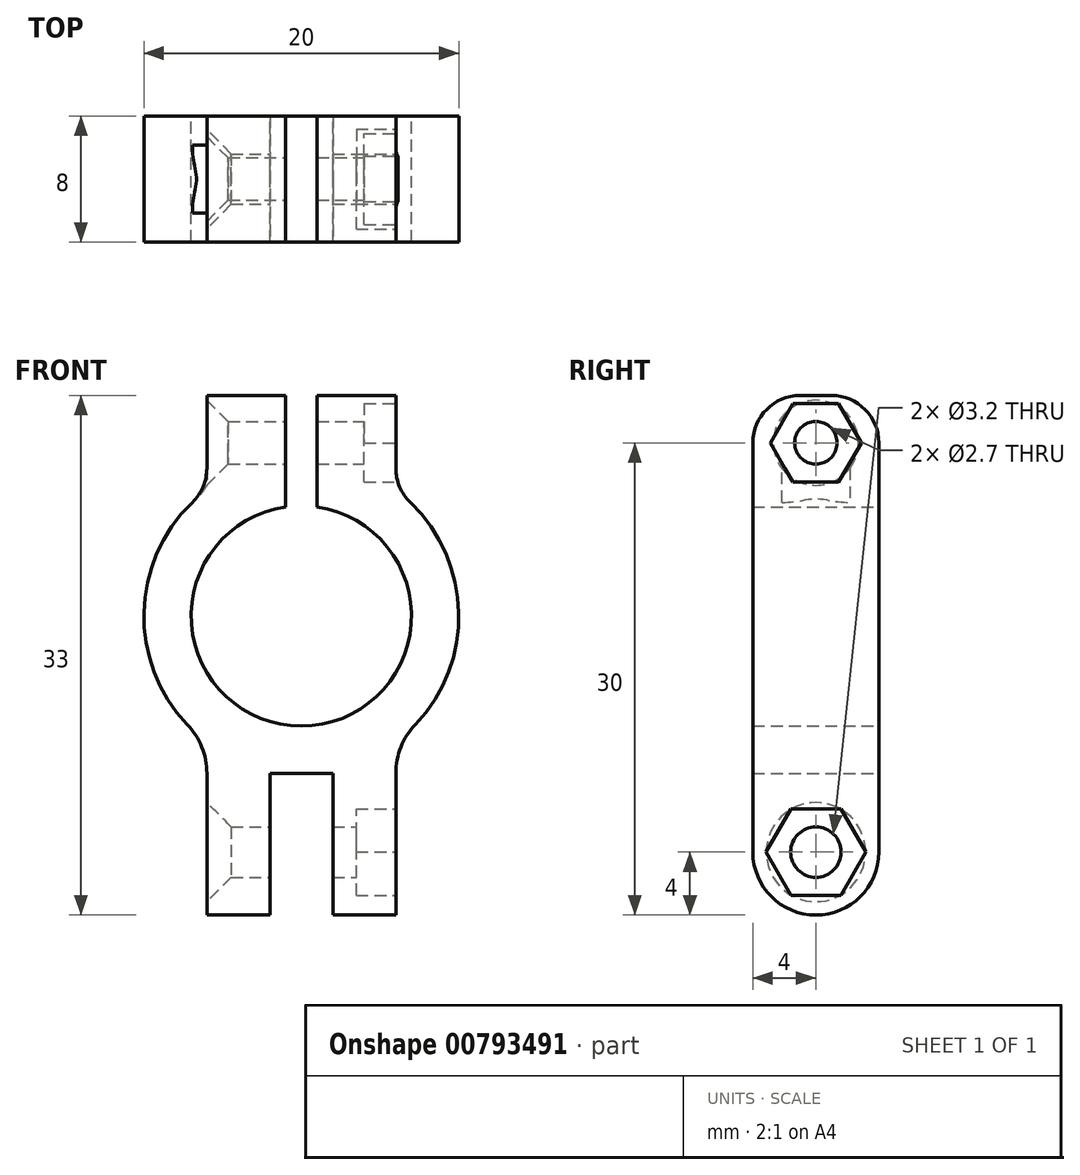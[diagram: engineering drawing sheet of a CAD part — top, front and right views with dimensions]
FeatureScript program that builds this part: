
annotation { "Feature Type Name" : "Feature", "Feature Type Description" : "" }
export const myFeature = defineFeature(function(context is Context, id is Id, definition is map)
    precondition{}
    {
        {
            var Q0;
            Q0=qCreatedBy(makeId("Front.planeOp"),FACE);
            var sketch = newSketch(context, id + "F0", { "sketchPlane" : qUnion([Q0])});
            skLineSegment(sketch, "E0", {"start": v(-1, 14) * mm, "end": v(-1, 6.93) * mm});
            skLineSegment(sketch, "E1.trimOffspring", {"start": v(-1, 14) * mm, "end": v(-6, 14) * mm});
            skLineSegment(sketch, "E2", {"start": v(-6, -19) * mm, "end": v(-2, -19) * mm});
            skLineSegment(sketch, "E3", {"start": v(-2, -19) * mm, "end": v(-2, -10) * mm});
            skLineSegment(sketch, "E4", {"start": v(-6, -19) * mm, "end": v(-6, -10) * mm});
            skArc(sketch, "E5", {"start": v(-6, -10) * mm, "mid": v(-6.32, -8.33) * mm, "end": v(-7.24, -6.9) * mm});
            skLineSegment(sketch, "E6", {"start": v(-6, -10) * mm, "end": v(-10.5, -10) * mm, "construction": true});
            skLineSegment(sketch, "E7.MirrorCS", {"start": v(2, -19) * mm, "end": v(2, -10) * mm});
            skLineSegment(sketch, "E8.MirrorCS", {"start": v(6, -19) * mm, "end": v(6, -10) * mm});
            skLineSegment(sketch, "E9.MirrorCS", {"start": v(6, -19) * mm, "end": v(2, -19) * mm});
            skArc(sketch, "E10.MirrorCS", {"start": v(6, -10) * mm, "mid": v(6.32, -8.33) * mm, "end": v(7.24, -6.9) * mm});
            skLineSegment(sketch, "E11", {"start": v(-2, -10) * mm, "end": v(2, -10) * mm});
            skLineSegment(sketch, "E12", {"start": v(-6, 14) * mm, "end": v(-6, 8) * mm});
            skArc(sketch, "E13", {"start": v(-7.24, -6.9) * mm, "mid": v(-9.97, 0.83) * mm, "end": v(-6, 8) * mm});
            skLineSegment(sketch, "E14.MirrorCS", {"start": v(6, 14) * mm, "end": v(6, 8) * mm});
            skArc(sketch, "E15.MirrorCS", {"start": v(7.24, -6.9) * mm, "mid": v(9.97, 0.83) * mm, "end": v(6, 8) * mm});
            skLineSegment(sketch, "E16.MirrorCS", {"start": v(1, 14) * mm, "end": v(1, 6.93) * mm});
            skLineSegment(sketch, "E17.MirrorCS", {"start": v(1, 14) * mm, "end": v(6, 14) * mm});
            skArc(sketch, "E18", {"start": v(-1, 6.93) * mm, "mid": v(0, -7) * mm, "end": v(1, 6.93) * mm});
            skSolve(sketch);
        }
        {
            var Q0;
            Q0=makeQuery(id+"F0.imprint","IMPRINT",FACE,{"disambiguationData":[TD([[makeQuery(id+"F0.imprint","IMPRINT",EDGE,{"derivedFrom":sQuery(id+"F0.wireOp",EDGE,"E0")}),-1.0]])]});
            extrude(context, id + "F1", {"entities" : qUnion([Q0]), "endBound" : BoundingType.SYMMETRIC, "depth" : 8 * mm, "offsetDistance" : 25 * mm});
        }
        {
            var Q0;
            Q0=makeQuery(id+"F1.opExtrude","SWEPT_FACE",FACE,{"disambiguationData":[OSD([sQuery(id+"F0.wireOp",EDGE,"E14.MirrorCS")])]});
            var sketch = newSketch(context, id + "F2", { "sketchPlane" : qUnion([Q0])});
            skCircle(sketch, "E19", {"center": v(0, 11) * mm, "radius": 1.35 * mm});
            skCircle(sketch, "E20.cCircle", {"center": v(0, 11) * mm, "radius": 2.5 * mm, "construction": true});
            skLineSegment(sketch, "E20.0", {"start": v(1.44, 13.5) * mm, "end": v(2.89, 11) * mm});
            skLineSegment(sketch, "E20.1", {"start": v(2.89, 11) * mm, "end": v(1.44, 8.5) * mm});
            skLineSegment(sketch, "E20.2", {"start": v(1.44, 8.5) * mm, "end": v(-1.44, 8.5) * mm});
            skLineSegment(sketch, "E20.3", {"start": v(-1.44, 8.5) * mm, "end": v(-2.89, 11) * mm});
            skLineSegment(sketch, "E20.4", {"start": v(-2.89, 11) * mm, "end": v(-1.44, 13.5) * mm});
            skLineSegment(sketch, "E20.5", {"start": v(-1.44, 13.5) * mm, "end": v(1.44, 13.5) * mm});
            skPoint(sketch, "E20.0.midPoint", {"position": v(2.17, 12.25) * mm});
            skSolve(sketch);
        }
        {
            var Q0;
            Q0=makeQuery(id+"F2.imprint","IMPRINT",FACE,{"disambiguationData":[TD([[makeQuery(id+"F2.imprint","IMPRINT",EDGE,{"derivedFrom":sQuery(id+"F2.wireOp",EDGE,"E19")}),1.0]])]});
            var Q1;
            {var subQ0=sQuery(id+"F2.wireOp",EDGE,"nRwaLtps-0aPM-k6Bh-PqO4-CJdIWXvHlXeP");Q1=makeQuery(id+"F2.imprint","IMPRINT",FACE,{"disambiguationData":[TD([[makeQuery(id+"F2.imprint","IMPRINT",EDGE,{"derivedFrom":subQ0}),1.0]])]});}
            var Q2;
            {var subQ0=sQuery(id+"F2.wireOp",EDGE,"26d730cf-6a02-49fb-9eb9-cb2f17dd4a160.MirrorCS");Q2=makeQuery(id+"F2.imprint","IMPRINT",FACE,{"disambiguationData":[TD([[makeQuery(id+"F2.imprint","IMPRINT",EDGE,{"derivedFrom":subQ0}),-1.0]])]});}
            extrude(context, id + "F3", {"entities" : qUnion([Q0, Q1, Q2]), "operationType" : NewBodyOperationType.REMOVE, "oppositeDirection" : true, "depth" : 25 * mm, "offsetDistance" : 25 * mm});
        }
        {
            var Q0;
            Q0=makeQuery(id+"F2.imprint","IMPRINT",FACE,{"disambiguationData":[TD([[makeQuery(id+"F2.imprint","IMPRINT",EDGE,{"derivedFrom":sQuery(id+"F2.wireOp",EDGE,"E19")}),-1.0]])]});
            extrude(context, id + "F4", {"entities" : qUnion([Q0]), "operationType" : NewBodyOperationType.REMOVE, "oppositeDirection" : true, "depth" : 2 * mm, "offsetDistance" : 25 * mm});
        }
        {
            var Q0;
            Q0=makeQuery(id+"F1.opExtrude","SWEPT_FACE",FACE,{"disambiguationData":[OSD([sQuery(id+"F0.wireOp",EDGE,"E8.MirrorCS")])]});
            var sketch = newSketch(context, id + "F5", { "sketchPlane" : qUnion([Q0])});
            skCircle(sketch, "E21", {"center": v(0, -15) * mm, "radius": 1.6 * mm});
            skCircle(sketch, "E22.cCircle", {"center": v(0, -15) * mm, "radius": 2.75 * mm, "construction": true});
            skLineSegment(sketch, "E22.0", {"start": v(-1.59, -12.25) * mm, "end": v(1.59, -12.25) * mm});
            skLineSegment(sketch, "E22.1", {"start": v(1.59, -12.25) * mm, "end": v(3.18, -15) * mm});
            skLineSegment(sketch, "E22.2", {"start": v(3.18, -15) * mm, "end": v(1.59, -17.75) * mm});
            skLineSegment(sketch, "E22.3", {"start": v(1.59, -17.75) * mm, "end": v(-1.59, -17.75) * mm});
            skLineSegment(sketch, "E22.4", {"start": v(-1.59, -17.75) * mm, "end": v(-3.18, -15) * mm});
            skLineSegment(sketch, "E22.5", {"start": v(-3.18, -15) * mm, "end": v(-1.59, -12.25) * mm});
            skPoint(sketch, "E22.0.midPoint", {"position": v(0, -12.25) * mm});
            skSolve(sketch);
        }
        {
            var Q0;
            Q0=makeQuery(id+"F5.imprint","IMPRINT",FACE,{"disambiguationData":[TD([[makeQuery(id+"F5.imprint","IMPRINT",EDGE,{"derivedFrom":sQuery(id+"F5.wireOp",EDGE,"E21")}),1.0]])]});
            var Q1;
            {var subQ0=sQuery(id+"F5.wireOp",EDGE,"dgfmRsRT-HZR4-KMtm-UVD4-OGYZ9sb2hiea");var subQ1=sQuery(id+"F0.wireOp",EDGE,"URoOaodK-mer2-KlBf-KcxF-PiR6j1BPeDQ6");var subQ2=makeQuery(id+"F1.opExtrude","CAP_EDGE",EDGE,{"disambiguationData":[OSD([subQ1])],"isStart":false});var subQ3=makeQuery(id+"F5.imprint","INTERSECT",VERTEX,{"derivedFrom":[subQ2,sQuery(id+"F5.wireOp",EDGE,"iwAXt04E-8AKp-sdOK-APD1-idUJ9iq6WJ0X"),subQ0]});Q1=makeQuery(id+"F5.imprint","IMPRINT",FACE,{"disambiguationData":[TD([[makeQuery(id+"F5.imprint","IMPRINT",EDGE,{"disambiguationData":[TD([[subQ3,-1.0]])],"derivedFrom":subQ0}),-1.0]])]});}
            var Q2;
            {var subQ0=sQuery(id+"F5.wireOp",EDGE,"dgfmRsRT-HZR4-KMtm-UVD4-OGYZ9sb2hiea");var subQ1=sQuery(id+"F0.wireOp",EDGE,"URoOaodK-mer2-KlBf-KcxF-PiR6j1BPeDQ6");var subQ2=makeQuery(id+"F1.opExtrude","CAP_EDGE",EDGE,{"disambiguationData":[OSD([subQ1])],"isStart":true});var subQ3=makeQuery(id+"F5.imprint","INTERSECT",VERTEX,{"derivedFrom":[subQ2,sQuery(id+"F5.wireOp",EDGE,"2524a595-133a-427d-9363-88fda697d8180.MirrorCS"),subQ0]});Q2=makeQuery(id+"F5.imprint","IMPRINT",FACE,{"disambiguationData":[TD([[makeQuery(id+"F5.imprint","IMPRINT",EDGE,{"disambiguationData":[TD([[subQ3,1.0]])],"derivedFrom":subQ0}),-1.0]])]});}
            extrude(context, id + "F6", {"entities" : qUnion([Q0, Q1, Q2]), "operationType" : NewBodyOperationType.REMOVE, "oppositeDirection" : true, "depth" : 25 * mm, "offsetDistance" : 25 * mm});
        }
        {
            var Q0;
            Q0=makeQuery(id+"F5.imprint","IMPRINT",FACE,{"disambiguationData":[TD([[makeQuery(id+"F5.imprint","IMPRINT",EDGE,{"derivedFrom":sQuery(id+"F5.wireOp",EDGE,"E21")}),-1.0]])]});
            extrude(context, id + "F7", {"entities" : qUnion([Q0]), "operationType" : NewBodyOperationType.REMOVE, "oppositeDirection" : true, "depth" : 2.5 * mm, "offsetDistance" : 25 * mm});
        }
        {
            var Q0;
            Q0=makeQuery(id+"F3.boolean.opBoolean","INTERSECT",EDGE,{"derivedFrom":[makeQuery(id+"F1.opExtrude","SWEPT_FACE",FACE,{"disambiguationData":[OSD([sQuery(id+"F0.wireOp",EDGE,"E12")])]}),makeQuery(id+"F3.opExtrude","SWEPT_FACE",FACE,{"disambiguationData":[OSD([sQuery(id+"F2.wireOp",EDGE,"E19")])]})]});
            chamfer(context, id + "F8", {"entities" : qUnion([Q0]), "width" : 1.35 * mm, "tangentPropagation" : true});
        }
        {
            var Q0;
            Q0=makeQuery(id+"F6.boolean.opBoolean","INTERSECT",EDGE,{"derivedFrom":[makeQuery(id+"F1.opExtrude","SWEPT_FACE",FACE,{"disambiguationData":[OSD([sQuery(id+"F0.wireOp",EDGE,"E4")])]}),makeQuery(id+"F6.opExtrude","SWEPT_FACE",FACE,{"disambiguationData":[OSD([sQuery(id+"F5.wireOp",EDGE,"E21")])]})]});
            chamfer(context, id + "F9", {"entities" : qUnion([Q0]), "width" : 1.55 * mm, "tangentPropagation" : true});
        }
        {
            var Q0;
            Q0=makeQuery(id+"F1.opExtrude","CAP_EDGE",EDGE,{"disambiguationData":[OSD([sQuery(id+"F0.wireOp",EDGE,"E9.MirrorCS")])],"isStart":false});
            var Q1;
            Q1=makeQuery(id+"F1.opExtrude","CAP_EDGE",EDGE,{"disambiguationData":[OSD([sQuery(id+"F0.wireOp",EDGE,"E2")])],"isStart":false});
            var Q2;
            Q2=makeQuery(id+"F1.opExtrude","CAP_EDGE",EDGE,{"disambiguationData":[OSD([sQuery(id+"F0.wireOp",EDGE,"E2")])],"isStart":true});
            var Q3;
            Q3=makeQuery(id+"F1.opExtrude","CAP_EDGE",EDGE,{"disambiguationData":[OSD([sQuery(id+"F0.wireOp",EDGE,"E9.MirrorCS")])],"isStart":true});
            fillet(context, id + "F10", {"entities" : qUnion([Q0, Q1, Q2, Q3]), "radius" : 4 * mm, "tangentPropagation" : true, "allowEdgeOverflow" : false});
        }
        {
            var Q0;
            Q0=makeQuery(id+"F1.opExtrude","CAP_EDGE",EDGE,{"disambiguationData":[OSD([sQuery(id+"F0.wireOp",EDGE,"E1.trimOffspring")])],"isStart":false});
            var Q1;
            Q1=makeQuery(id+"F1.opExtrude","CAP_EDGE",EDGE,{"disambiguationData":[OSD([sQuery(id+"F0.wireOp",EDGE,"E17.MirrorCS")])],"isStart":false});
            var Q2;
            Q2=makeQuery(id+"F1.opExtrude","CAP_EDGE",EDGE,{"disambiguationData":[OSD([sQuery(id+"F0.wireOp",EDGE,"E1.trimOffspring")])],"isStart":true});
            var Q3;
            Q3=makeQuery(id+"F1.opExtrude","CAP_EDGE",EDGE,{"disambiguationData":[OSD([sQuery(id+"F0.wireOp",EDGE,"E17.MirrorCS")])],"isStart":true});
            var Q4;
            Q4=makeQuery(id+"F1.opExtrude","SWEPT_EDGE",EDGE,{"disambiguationData":[OSD([sQuery(id+"F0.wireOp",EDGE,"E14.MirrorCS"),sQuery(id+"F0.wireOp",EDGE,"E15.MirrorCS")])]});
            var Q5;
            Q5=makeQuery(id+"F1.opExtrude","SWEPT_EDGE",EDGE,{"disambiguationData":[OSD([sQuery(id+"F0.wireOp",EDGE,"E12"),sQuery(id+"F0.wireOp",EDGE,"E13")])]});
            fillet(context, id + "F11", {"entities" : qUnion([Q0, Q1, Q2, Q3, Q4, Q5]), "radius" : 3 * mm, "tangentPropagation" : true, "allowEdgeOverflow" : false});
        }
    });
